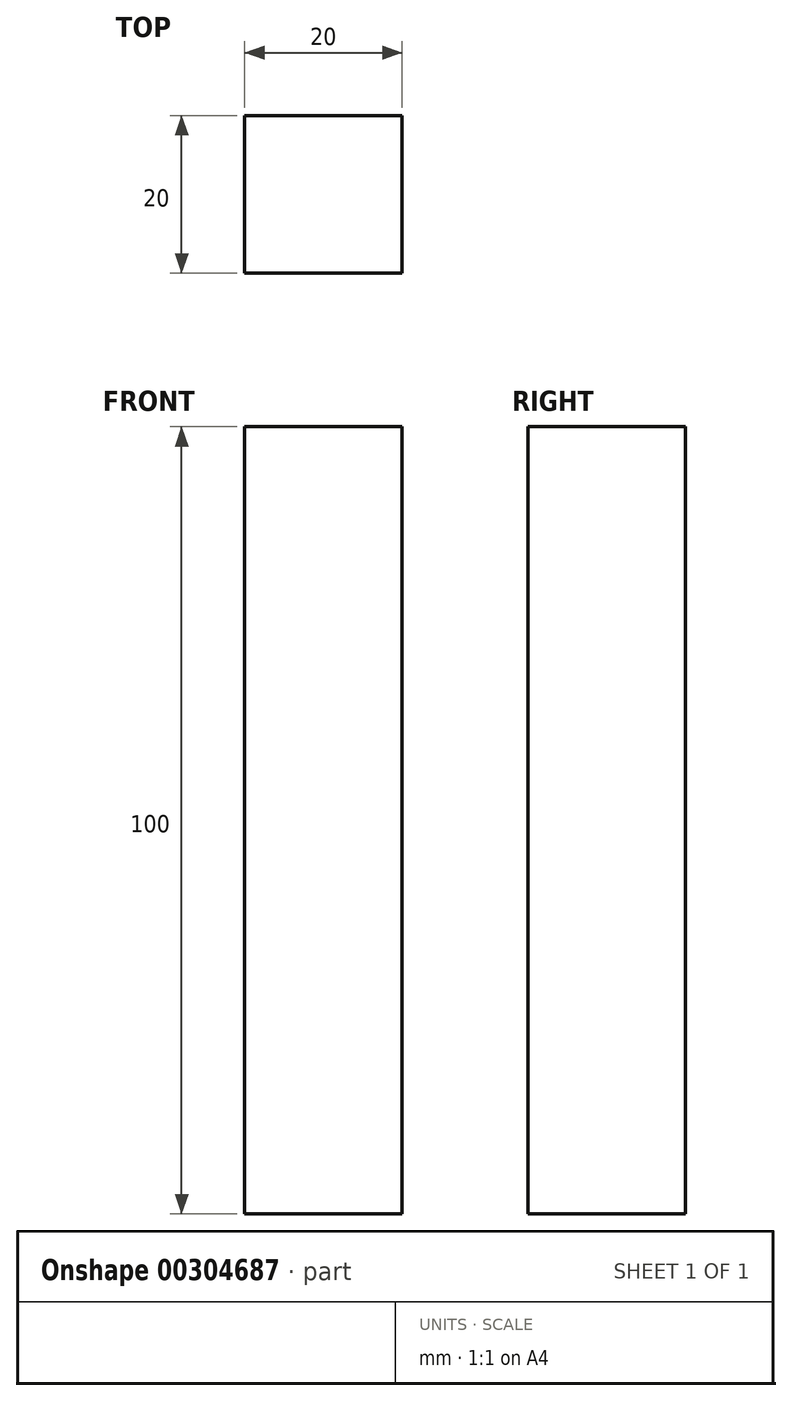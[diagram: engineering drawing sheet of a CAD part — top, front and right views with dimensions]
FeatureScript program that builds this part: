
annotation { "Feature Type Name" : "Feature", "Feature Type Description" : "" }
export const myFeature = defineFeature(function(context is Context, id is Id, definition is map)
    precondition{}
    {
        {
            var Q0;
            Q0=qCreatedBy(makeId("Top.planeOp"),FACE);
            var sketch = newSketch(context, id + "F0", { "sketchPlane" : qUnion([Q0])});
            skLineSegment(sketch, "E0.bottom", {"start": v(10, 10) * mm, "end": v(-10, 10) * mm});
            skLineSegment(sketch, "E0.top", {"start": v(10, -10) * mm, "end": v(-10, -10) * mm});
            skLineSegment(sketch, "E0.left", {"start": v(10, 10) * mm, "end": v(10, -10) * mm});
            skLineSegment(sketch, "E0.right", {"start": v(-10, 10) * mm, "end": v(-10, -10) * mm});
            skPoint(sketch, "E0.middle", {"position": v(0, 0) * mm});
            skSolve(sketch);
        }
        {
            var Q0;
            Q0 = qSketchRegion(id + "F0", true);
            extrude(context, id + "F1", {"entities" : qUnion([Q0]), "depth" : 100 * mm});
        }
    });
